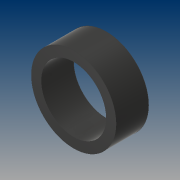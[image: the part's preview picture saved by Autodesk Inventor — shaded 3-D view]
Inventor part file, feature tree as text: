
AUTODESK INVENTOR PART (.ipt)
format: ipt  version: 2021 (Build 250183000, 183)  size: 103,424 bytes
history: native  units: mm
features: extrude x1, sketch x1
ambient origin geometry x8: Origin, YZ Plane, XZ Plane, XY Plane, X Axis, Y Axis, Z Axis, Center Point
bodies: Solid1 (feature_tree)
feature tree (2):
  extrude  "Extrusion1"  Depth=10.0mm
  sketch  "Sketch1"  dims[d0=20.0mm d1=26.0mm d2=10.0mm d3=0.0mm]
